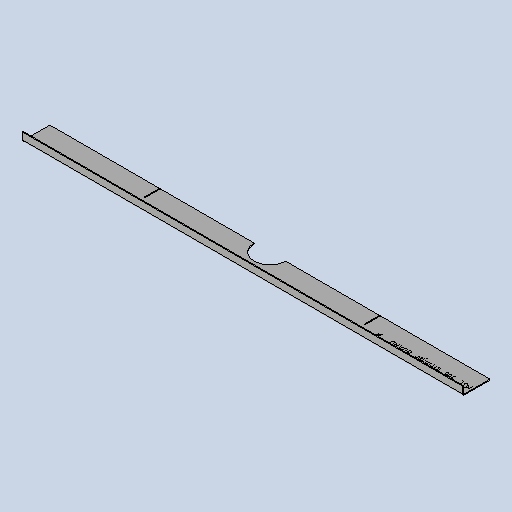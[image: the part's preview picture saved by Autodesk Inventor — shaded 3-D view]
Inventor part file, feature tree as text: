
AUTODESK INVENTOR PART (.ipt)
format: ipt  version: 2025 (Build 290162010, 162A)  size: 297,984 bytes
history: native  units: mm
features: other x5, sheet_metal_op x4, sketch x4, extrude x1
ambient origin geometry x8: Origin, YZ Plane, XZ Plane, XY Plane, X Axis, Y Axis, Z Axis, Center Point
bodies: Solid1 (feature_tree)
feature tree (14):
  sheet_metal_op  "Face1"
  sheet_metal_op  "Flange1"
  extrude  "Extrusion1"  Depth=62.0mm
  other  "Mark2"
  other  "A-Side Definition"
  sketch  "Sketch1"  dims[d0=980.0mm d1=62.0mm]
  other  "Plate1"
  sketch  "Sketch2"  dims[d2=2.0mm]
  other  "Plate2"
  sheet_metal_op  "Bend1"
  sheet_metal_op  "Corner1"
  sketch  "Sketch5"  dims[d3=2.0mm]
  sketch  "Sketch9"  dims[d4=1.0mm d5=4.0mm d6=2.75mm d7=20.0mm d8=90.0deg d9=2.75mm d10=8.0mm d11=2.0mm d12=2.75mm d15=0.0mm d16=0.0mm d40=200.0mm d41=12.0mm d45=70.0mm d48=2.1mm d49=490.0mm d51=29.0mm d52=33.0mm]
  other  "Definition1"
